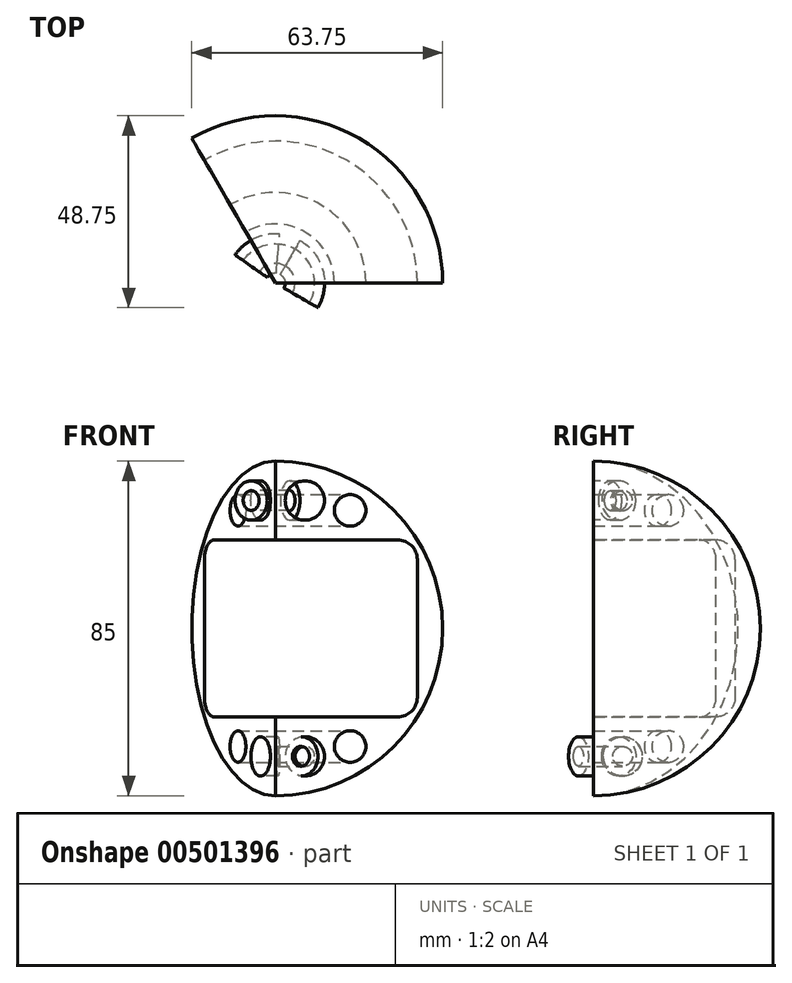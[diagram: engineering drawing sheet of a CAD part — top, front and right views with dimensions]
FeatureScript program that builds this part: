
annotation { "Feature Type Name" : "Feature", "Feature Type Description" : "" }
export const myFeature = defineFeature(function(context is Context, id is Id, definition is map)
    precondition{}
    {
        {
            var Q0;
            Q0=qCreatedBy(makeId("Front.planeOp"),FACE);
            var sketch = newSketch(context, id + "F0", { "sketchPlane" : qUnion([Q0])});
            skArc(sketch, "E0", {"start": v(0, -45) * mm, "mid": v(45, 0) * mm, "end": v(0, 45) * mm});
            skArc(sketch, "E1", {"start": v(0, -42.5) * mm, "mid": v(42.5, 0) * mm, "end": v(0, 42.5) * mm});
            skLineSegment(sketch, "E2", {"start": v(0, 42.5) * mm, "end": v(0, 45) * mm});
            skLineSegment(sketch, "E3", {"start": v(0, -45) * mm, "end": v(0, -42.5) * mm});
            skLineSegment(sketch, "E4", {"start": v(0, 42.5) * mm, "end": v(0, 22.5) * mm});
            skLineSegment(sketch, "E5", {"start": v(0, 22.5) * mm, "end": v(31.06, 22.5) * mm});
            skLineSegment(sketch, "E6", {"start": v(36.06, -17.5) * mm, "end": v(36.06, 17.5) * mm});
            skLineSegment(sketch, "E7", {"start": v(0, -42.5) * mm, "end": v(0, -22.5) * mm});
            skLineSegment(sketch, "E8", {"start": v(0, -22.5) * mm, "end": v(31.06, -22.5) * mm});
            skPoint(sketch, "E9.visualSharp", {"position": v(36.06, 22.5) * mm});
            skArc(sketch, "E9.filletArc", {"start": v(36.06, 17.5) * mm, "mid": v(34.6, 21.04) * mm, "end": v(31.06, 22.5) * mm});
            skPoint(sketch, "E10.visualSharp", {"position": v(36.06, -22.5) * mm});
            skArc(sketch, "E10.filletArc", {"start": v(31.06, -22.5) * mm, "mid": v(34.6, -21.04) * mm, "end": v(36.06, -17.5) * mm});
            skSolve(sketch);
        }
        {
            var Q0;
            Q0=makeQuery(id+"F0.imprint","IMPRINT",FACE,{"disambiguationData":[TD([[makeQuery(id+"F0.imprint","IMPRINT",EDGE,{"derivedFrom":sQuery(id+"F0.wireOp",EDGE,"E1")}),1.0]])]});
            var Q1;
            Q1=sQuery(id+"F0.wireOp",EDGE,"E5");
            var Q2;
            Q2=sQuery(id+"F0.wireOp",EDGE,"E4");
            var Q3;
            Q3=sQuery(id+"F0.wireOp",EDGE,"E1");
            var Q4;
            Q4=sQuery(id+"F0.wireOp",EDGE,"E6");
            var Q5;
            Q5=sQuery(id+"F0.wireOp",EDGE,"E9.filletArc");
            var Q6;
            Q6=sQuery(id+"F0.wireOp",EDGE,"E10.filletArc");
            var Q7;
            Q7=sQuery(id+"F0.wireOp",EDGE,"E8");
            var Q8;
            Q8=sQuery(id+"F0.wireOp",EDGE,"E7");
            var Q9;
            Q9=sQuery(id+"F0.wireOp",EDGE,"E7");
            revolve(context, id + "F1", {"entities" : qUnion([Q0]), "surfaceEntities" : qUnion([Q1, Q2, Q3, Q4, Q5, Q6, Q7, Q8]), "axis" : qUnion([Q9]), "revolveType" : RevolveType.ONE_DIRECTION, "angle" : 120 * degree});
        }
        {
            var Q0;
            Q0=makeQuery(id+"F1.opRevolve","CAP_FACE",FACE,{"disambiguationData":[OSD([sQuery(id+"F0.wireOp",EDGE,"E1"),sQuery(id+"F0.wireOp",EDGE,"E4"),sQuery(id+"F0.wireOp",EDGE,"E5"),sQuery(id+"F0.wireOp",EDGE,"E6"),sQuery(id+"F0.wireOp",EDGE,"E7"),sQuery(id+"F0.wireOp",EDGE,"E8"),sQuery(id+"F0.wireOp",EDGE,"E9.filletArc"),sQuery(id+"F0.wireOp",EDGE,"E10.filletArc")])],"isStart":true});
            var sketch = newSketch(context, id + "F2", { "sketchPlane" : qUnion([Q0])});
            skCircle(sketch, "E11", {"center": v(7.5, 32.5) * mm, "radius": 5 * mm});
            skPoint(sketch, "E11.centerSnap0", {"position": v(0, 32.5) * mm});
            skSolve(sketch);
        }
        {
            var Q0;
            Q0=makeQuery(id+"F2.imprint","IMPRINT",FACE,{"disambiguationData":[TD([[makeQuery(id+"F2.imprint","IMPRINT",EDGE,{"derivedFrom":sQuery(id+"F2.wireOp",EDGE,"E11")}),1.0]])]});
            var Q1;
            Q1=makeQuery(id+"F1.opRevolve","CAP_EDGE",EDGE,{"disambiguationData":[OSD([sQuery(id+"F0.wireOp",EDGE,"E4")])],"isStart":true});
            revolve(context, id + "F3", {"operationType" : NewBodyOperationType.REMOVE, "entities" : qUnion([Q0]), "axis" : qUnion([Q1]), "revolveType" : RevolveType.ONE_DIRECTION, "oppositeDirection" : true, "angle" : 60 * degree});
        }
        {
            var Q0;
            Q0=makeQuery(id+"F1.opRevolve","CAP_FACE",FACE,{"disambiguationData":[OSD([sQuery(id+"F0.wireOp",EDGE,"E1"),sQuery(id+"F0.wireOp",EDGE,"E4"),sQuery(id+"F0.wireOp",EDGE,"E5"),sQuery(id+"F0.wireOp",EDGE,"E6"),sQuery(id+"F0.wireOp",EDGE,"E7"),sQuery(id+"F0.wireOp",EDGE,"E8"),sQuery(id+"F0.wireOp",EDGE,"E9.filletArc"),sQuery(id+"F0.wireOp",EDGE,"E10.filletArc")])],"isStart":false});
            var sketch = newSketch(context, id + "F4", { "sketchPlane" : qUnion([Q0])});
            skCircle(sketch, "E12", {"center": v(-7.5, 32.5) * mm, "radius": 5 * mm});
            skPoint(sketch, "E12.centerSnap0", {"position": v(0, 32.5) * mm});
            skSolve(sketch);
        }
        {
            var Q0;
            Q0=makeQuery(id+"F4.imprint","IMPRINT",FACE,{"disambiguationData":[TD([[makeQuery(id+"F4.imprint","IMPRINT",EDGE,{"derivedFrom":sQuery(id+"F4.wireOp",EDGE,"E12")}),1.0]])]});
            var Q1;
            Q1=makeQuery(id+"F1.opRevolve","CAP_EDGE",EDGE,{"disambiguationData":[OSD([sQuery(id+"F0.wireOp",EDGE,"E4")])],"isStart":true});
            revolve(context, id + "F5", {"operationType" : NewBodyOperationType.ADD, "entities" : qUnion([Q0]), "axis" : qUnion([Q1]), "revolveType" : RevolveType.ONE_DIRECTION, "oppositeDirection" : true, "angle" : 25 * degree});
        }
        {
            var Q0;
            Q0=makeQuery(id+"F1.opRevolve","CAP_FACE",FACE,{"disambiguationData":[OSD([sQuery(id+"F0.wireOp",EDGE,"E1"),sQuery(id+"F0.wireOp",EDGE,"E4"),sQuery(id+"F0.wireOp",EDGE,"E5"),sQuery(id+"F0.wireOp",EDGE,"E6"),sQuery(id+"F0.wireOp",EDGE,"E7"),sQuery(id+"F0.wireOp",EDGE,"E8"),sQuery(id+"F0.wireOp",EDGE,"E9.filletArc"),sQuery(id+"F0.wireOp",EDGE,"E10.filletArc")])],"isStart":false});
            var sketch = newSketch(context, id + "F6", { "sketchPlane" : qUnion([Q0])});
            skCircle(sketch, "E13", {"center": v(-7.5, -32.5) * mm, "radius": 5 * mm});
            skPoint(sketch, "E13.centerSnap0", {"position": v(0, -32.5) * mm});
            skSolve(sketch);
        }
        {
            var Q0;
            Q0=makeQuery(id+"F2.imprint","IMPRINT",FACE,{"disambiguationData":[TD([[makeQuery(id+"F2.imprint","IMPRINT",EDGE,{"derivedFrom":sQuery(id+"F2.wireOp",EDGE,"E11")}),-1.0]])]});
            var sketch = newSketch(context, id + "F7", { "sketchPlane" : qUnion([Q0])});
            skCircle(sketch, "E14", {"center": v(7.5, -32.5) * mm, "radius": 5 * mm});
            skSolve(sketch);
        }
        {
            var Q0;
            Q0=makeQuery(id+"F7.imprint","IMPRINT",FACE,{"disambiguationData":[TD([[makeQuery(id+"F7.imprint","IMPRINT",EDGE,{"derivedFrom":sQuery(id+"F7.wireOp",EDGE,"E14")}),1.0]])]});
            var Q1;
            Q1=makeQuery(id+"F1.opRevolve","CAP_EDGE",EDGE,{"disambiguationData":[OSD([sQuery(id+"F0.wireOp",EDGE,"E7")])],"isStart":true});
            revolve(context, id + "F8", {"operationType" : NewBodyOperationType.ADD, "entities" : qUnion([Q0]), "axis" : qUnion([Q1]), "revolveType" : RevolveType.ONE_DIRECTION, "oppositeDirection" : true, "angle" : 30 * degree});
        }
        {
            var Q0;
            Q0=makeQuery(id+"F6.imprint","IMPRINT",FACE,{"disambiguationData":[TD([[makeQuery(id+"F6.imprint","IMPRINT",EDGE,{"derivedFrom":sQuery(id+"F6.wireOp",EDGE,"E13")}),1.0]])]});
            var Q1;
            Q1=makeQuery(id+"F1.opRevolve","CAP_EDGE",EDGE,{"disambiguationData":[OSD([sQuery(id+"F0.wireOp",EDGE,"E7")])],"isStart":true});
            revolve(context, id + "F9", {"operationType" : NewBodyOperationType.REMOVE, "entities" : qUnion([Q0]), "axis" : qUnion([Q1]), "revolveType" : RevolveType.ONE_DIRECTION, "oppositeDirection" : true, "angle" : 35 * degree});
        }
        {
            var Q0;
            Q0=makeQuery(id+"F8.opRevolve","CAP_FACE",FACE,{"disambiguationData":[OSD([sQuery(id+"F7.wireOp",EDGE,"E14")])],"isStart":false});
            var sketch = newSketch(context, id + "F10", { "sketchPlane" : qUnion([Q0])});
            skCircle(sketch, "E15", {"center": v(7.5, -32.5) * mm, "radius": 2.5 * mm});
            skSolve(sketch);
        }
        {
            var Q0;
            Q0 = qSketchRegion(id + "F10", true);
            var Q1;
            Q1=makeQuery(id+"F1.opRevolve","CAP_EDGE",EDGE,{"disambiguationData":[OSD([sQuery(id+"F0.wireOp",EDGE,"E7")])],"isStart":true});
            revolve(context, id + "F11", {"operationType" : NewBodyOperationType.REMOVE, "entities" : qUnion([Q0]), "axis" : qUnion([Q1]), "revolveType" : RevolveType.FULL, "oppositeDirection" : true});
        }
        {
            var Q0;
            Q0=makeQuery(id+"F5.opRevolve","CAP_FACE",FACE,{"disambiguationData":[OSD([sQuery(id+"F4.wireOp",EDGE,"E12")])],"isStart":false});
            var sketch = newSketch(context, id + "F12", { "sketchPlane" : qUnion([Q0])});
            skCircle(sketch, "E16", {"center": v(-7.5, 32.5) * mm, "radius": 2.5 * mm});
            skSolve(sketch);
        }
        {
            var Q0;
            Q0 = qSketchRegion(id + "F12", true);
            var Q1;
            Q1=makeQuery(id+"F1.opRevolve","CAP_EDGE",EDGE,{"disambiguationData":[OSD([sQuery(id+"F0.wireOp",EDGE,"E4")])],"isStart":true});
            revolve(context, id + "F13", {"operationType" : NewBodyOperationType.REMOVE, "entities" : qUnion([Q0]), "axis" : qUnion([Q1]), "revolveType" : RevolveType.FULL, "oppositeDirection" : true});
        }
        {
            var Q0;
            Q0=makeQuery(id+"F2.imprint","IMPRINT",FACE,{"disambiguationData":[TD([[makeQuery(id+"F2.imprint","IMPRINT",EDGE,{"derivedFrom":sQuery(id+"F2.wireOp",EDGE,"E11")}),-1.0]])]});
            var sketch = newSketch(context, id + "F14", { "sketchPlane" : qUnion([Q0])});
            skCircle(sketch, "E17", {"center": v(19, -30) * mm, "radius": 4 * mm});
            skCircle(sketch, "E18", {"center": v(19, 30) * mm, "radius": 4 * mm});
            skSolve(sketch);
        }
        {
            var Q0;
            Q0 = qSketchRegion(id + "F14", true);
            var Q1;
            Q1=makeQuery(id+"F1.opRevolve","CAP_EDGE",EDGE,{"disambiguationData":[OSD([sQuery(id+"F0.wireOp",EDGE,"E7")])],"isStart":true});
            revolve(context, id + "F15", {"operationType" : NewBodyOperationType.REMOVE, "entities" : qUnion([Q0]), "axis" : qUnion([Q1]), "revolveType" : RevolveType.FULL, "oppositeDirection" : true});
        }
    });
